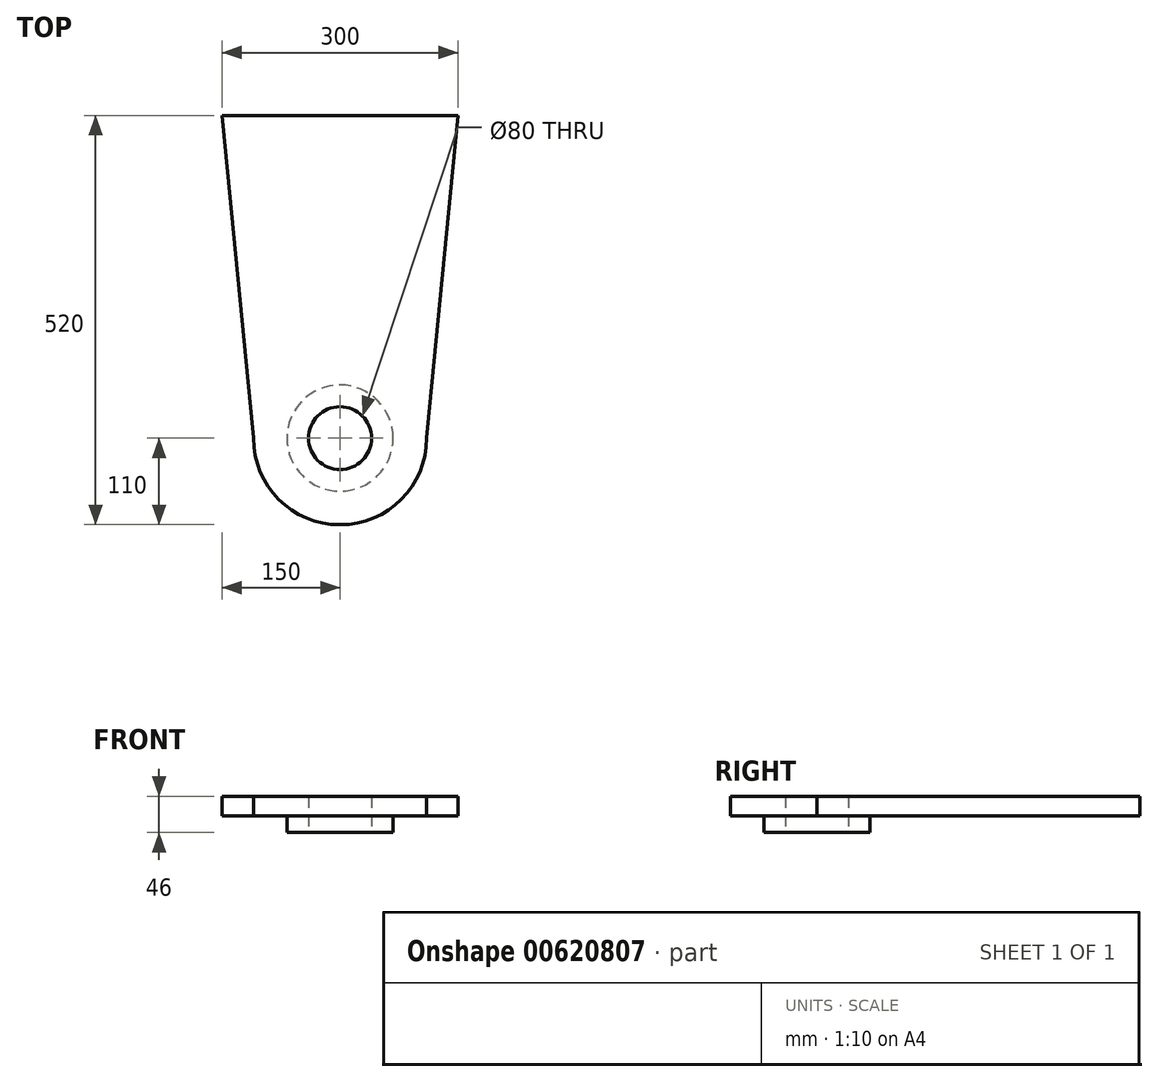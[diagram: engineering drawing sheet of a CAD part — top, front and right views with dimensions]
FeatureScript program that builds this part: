
annotation { "Feature Type Name" : "Feature", "Feature Type Description" : "" }
export const myFeature = defineFeature(function(context is Context, id is Id, definition is map)
    precondition{}
    {
        {
            var Q0;
            Q0=qCreatedBy(makeId("Top.planeOp"),FACE);
            var sketch = newSketch(context, id + "F0", { "sketchPlane" : qUnion([Q0])});
            skCircle(sketch, "E0", {"center": v(0, 0) * mm, "radius": 110 * mm});
            skSolve(sketch);
        }
        {
            var Q0;
            Q0 = qSketchRegion(id + "F0", true);
            extrude(context, id + "F1", {"entities" : qUnion([Q0]), "endBound" : BoundingType.SYMMETRIC, "depth" : 25 * mm, "offsetDistance" : 25 * mm});
        }
        {
            var Q0;
            Q0=makeQuery(id+"F1.opExtrude","CAP_FACE",FACE,{"disambiguationData":[OSD([sQuery(id+"F0.wireOp",EDGE,"E0")])],"isStart":false});
            var sketch = newSketch(context, id + "F2", { "sketchPlane" : qUnion([Q0])});
            skLineSegment(sketch, "E1", {"start": v(110, 0) * mm, "end": v(150, 410) * mm});
            skLineSegment(sketch, "E2", {"start": v(150, 410) * mm, "end": v(-150, 410) * mm});
            skLineSegment(sketch, "E3", {"start": v(-150, 410) * mm, "end": v(-110, 0) * mm});
            skLineSegment(sketch, "E4", {"start": v(-110, 0) * mm, "end": v(110, 0) * mm});
            skSolve(sketch);
        }
        {
            var Q0;
            Q0 = qSketchRegion(id + "F2", true);
            extrude(context, id + "F3", {"entities" : qUnion([Q0]), "operationType" : NewBodyOperationType.ADD, "oppositeDirection" : true, "depth" : 25 * mm, "offsetDistance" : 25 * mm});
        }
        {
            var Q0;
            Q0=makeQuery(id+"F3.boolean.opBoolean","MERGE",FACE,{"derivedFrom":[makeQuery(id+"F1.opExtrude","CAP_FACE",FACE,{"disambiguationData":[OSD([sQuery(id+"F0.wireOp",EDGE,"E0")])],"isStart":true}),makeQuery(id+"F3.opExtrude","CAP_FACE",FACE,{"disambiguationData":[OSD([sQuery(id+"F2.wireOp",EDGE,"E1"),sQuery(id+"F2.wireOp",EDGE,"E2"),sQuery(id+"F2.wireOp",EDGE,"E3"),sQuery(id+"F2.wireOp",EDGE,"E4")])],"isStart":false})]});
            var sketch = newSketch(context, id + "F4", { "sketchPlane" : qUnion([Q0])});
            skCircle(sketch, "E5", {"center": v(0, 0) * mm, "radius": 67.5 * mm});
            skSolve(sketch);
        }
        {
            var Q0;
            Q0 = qSketchRegion(id + "F4", true);
            extrude(context, id + "F5", {"entities" : qUnion([Q0]), "operationType" : NewBodyOperationType.ADD, "depth" : 21 * mm, "offsetDistance" : 25 * mm});
        }
        {
            var Q0;
            Q0=makeQuery(id+"F5.opExtrude","CAP_FACE",FACE,{"disambiguationData":[OSD([sQuery(id+"F4.wireOp",EDGE,"E5")])],"isStart":false});
            var sketch = newSketch(context, id + "F6", { "sketchPlane" : qUnion([Q0])});
            skCircle(sketch, "E6", {"center": v(0, 0) * mm, "radius": 40 * mm});
            skSolve(sketch);
        }
        {
            var Q0;
            Q0 = qSketchRegion(id + "F6", true);
            extrude(context, id + "F7", {"entities" : qUnion([Q0]), "operationType" : NewBodyOperationType.REMOVE, "oppositeDirection" : true, "depth" : 60 * mm, "offsetDistance" : 25 * mm});
        }
    });
